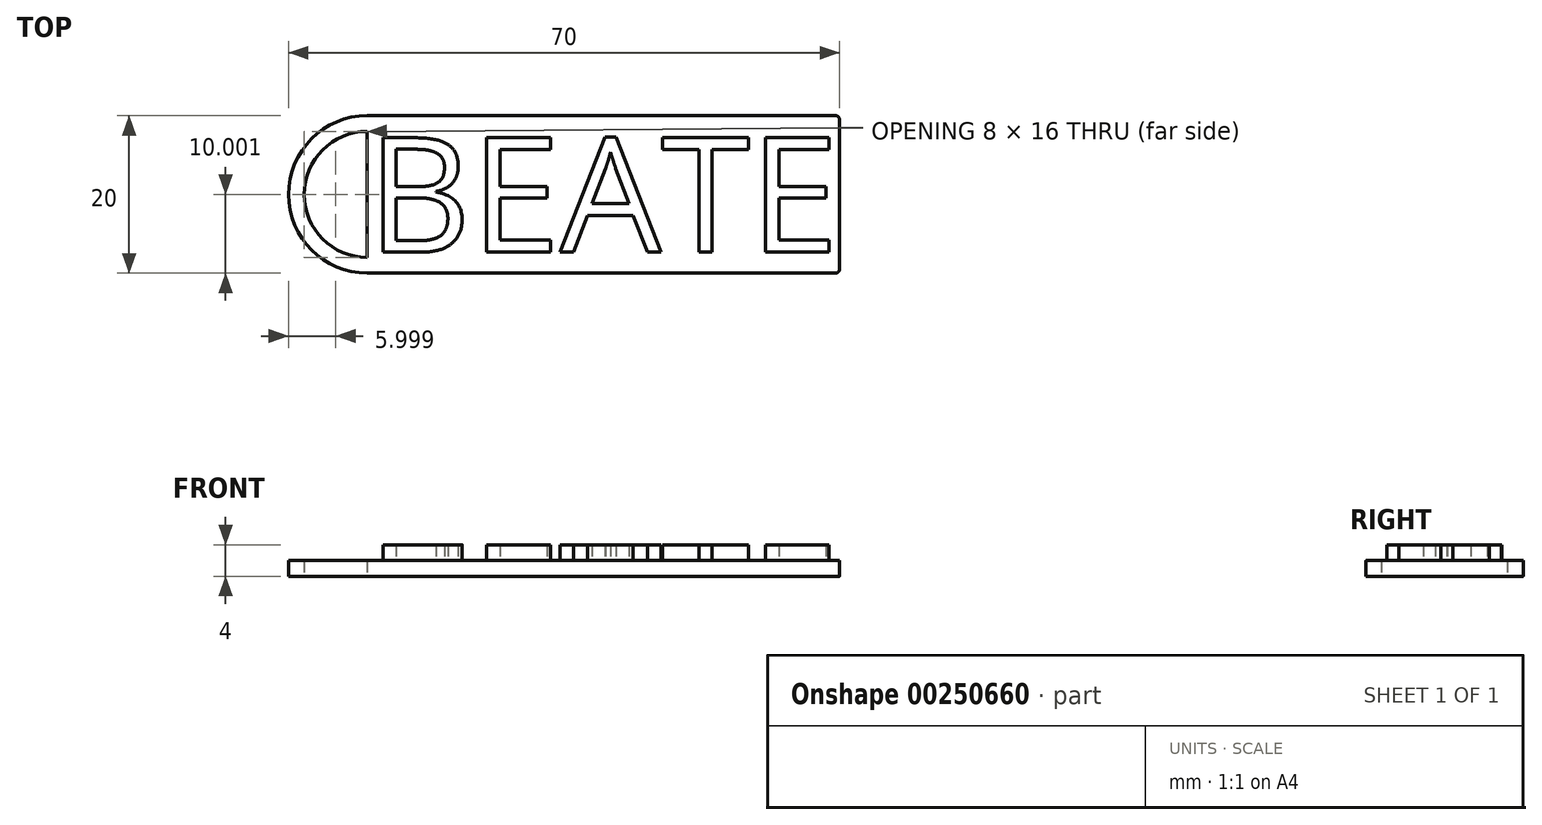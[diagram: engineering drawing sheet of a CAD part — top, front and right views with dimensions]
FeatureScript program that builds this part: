
annotation { "Feature Type Name" : "Feature", "Feature Type Description" : "" }
export const myFeature = defineFeature(function(context is Context, id is Id, definition is map)
    precondition{}
    {
        {
            var Q0;
            Q0=qCreatedBy(makeId("Top.planeOp"),FACE);
            var sketch = newSketch(context, id + "F0", { "sketchPlane" : qUnion([Q0])});
            skLineSegment(sketch, "E0.bottom", {"start": v(-5.27, 3.22) * mm, "end": v(54.73, 3.22) * mm});
            skLineSegment(sketch, "E0.top", {"start": v(-5.27, -16.78) * mm, "end": v(54.73, -16.78) * mm});
            skLineSegment(sketch, "E0.left", {"start": v(-5.27, 3.22) * mm, "end": v(-5.27, -16.78) * mm});
            skLineSegment(sketch, "E0.right", {"start": v(54.73, 3.22) * mm, "end": v(54.73, -16.78) * mm});
            skArc(sketch, "E1", {"start": v(-5.27, 3.22) * mm, "mid": v(-15.27, -6.78) * mm, "end": v(-5.27, -16.78) * mm});
            skArc(sketch, "E2", {"start": v(-5.27, 1.22) * mm, "mid": v(-13.27, -6.78) * mm, "end": v(-5.27, -14.78) * mm});
            skSolve(sketch);
        }
        {
            var Q0;
            Q0=qSketchRegion(id+"F0",true);
            extrude(context, id + "F4", {"entities" : qUnion([Q0]), "depth" : 2 * mm});
        }
        {
            var Q0;
            Q0=makeQuery(id+"F4.opExtrude","SWEPT_EDGE",EDGE,{"disambiguationData":[OSD([sQuery(id+"F0.wireOp",EDGE,"E0.top"),sQuery(id+"F0.wireOp",EDGE,"E0.right")])]});
            var Q1;
            Q1=makeQuery(id+"F4.opExtrude","SWEPT_EDGE",EDGE,{"disambiguationData":[OSD([sQuery(id+"F0.wireOp",EDGE,"E0.bottom"),sQuery(id+"F0.wireOp",EDGE,"E0.right")])]});
            fillet(context, id + "F1", {"entities" : qUnion([Q0, Q1]), "radius" : 0.5 * mm, "tangentPropagation" : true, "allowEdgeOverflow" : false});
        }
        {
            var Q0;
            Q0=makeQuery(id+"F4.opExtrude","CAP_FACE",FACE,{"disambiguationData":[OSD([sQuery(id+"F0.wireOp",EDGE,"E0.bottom"),sQuery(id+"F0.wireOp",EDGE,"E0.top"),sQuery(id+"F0.wireOp",EDGE,"E0.left"),sQuery(id+"F0.wireOp",EDGE,"E0.right"),sQuery(id+"F0.wireOp",EDGE,"E1"),sQuery(id+"F0.wireOp",EDGE,"E2")])],"isStart":false});
            var sketch = newSketch(context, id + "F2", { "sketchPlane" : qUnion([Q0])});
            skText(sketch, "E3", { "text": "BEATE", "fontName": "OpenSans-Regular.ttf"});
            skPoint(sketch, "E4", {"position": v(54.73, -6.78) * mm});
            skPoint(sketch, "E5", {"position": v(-5.27, -6.78) * mm});
            const initialGuessF2  = {"E3": [-0.00527, -0.0141, 1, 0, 0.01464]};
            skSetInitialGuess(sketch, initialGuessF2);
            skSolve(sketch);
        }
        {
            var Q0;
            Q0 = qSketchRegion(id + "F2", true);
            extrude(context, id + "F3", {"entities" : qUnion([Q0]), "operationType" : NewBodyOperationType.ADD, "depth" : 2 * mm});
        }
    });
